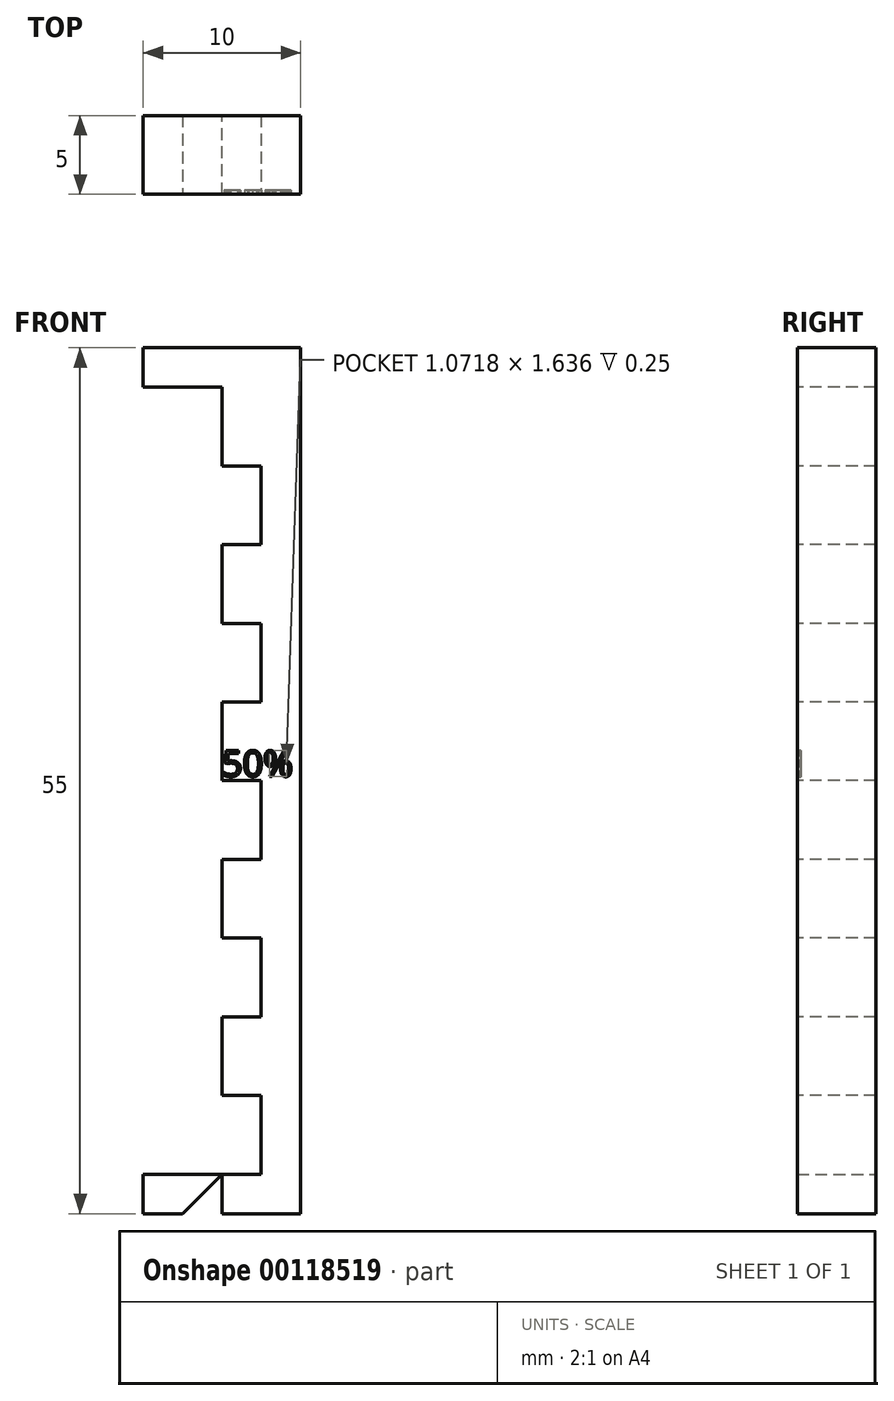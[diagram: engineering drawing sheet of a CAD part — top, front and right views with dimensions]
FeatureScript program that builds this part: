
annotation { "Feature Type Name" : "Feature", "Feature Type Description" : "" }
export const myFeature = defineFeature(function(context is Context, id is Id, definition is map)
    precondition{}
    {
        {
            var Q0;
            Q0=qCreatedBy(makeId("Front.planeOp"),FACE);
            var sketch = newSketch(context, id + "F0", { "sketchPlane" : qUnion([Q0])});
            skLineSegment(sketch, "E0.bottom", {"start": v(0, 10) * mm, "end": v(10, 10) * mm});
            skLineSegment(sketch, "E0.top", {"start": v(-10, -10) * mm, "end": v(10, -10) * mm});
            skLineSegment(sketch, "E0.left", {"start": v(-10, 0) * mm, "end": v(-10, -10) * mm});
            skLineSegment(sketch, "E0.right", {"start": v(10, 10) * mm, "end": v(10, -10) * mm});
            skLineSegment(sketch, "E1.top", {"start": v(-10, 0) * mm, "end": v(0, 0) * mm});
            skLineSegment(sketch, "E1.right", {"start": v(0, 10) * mm, "end": v(0, 0) * mm});
            skSolve(sketch);
        }
        {
            var Q0;
            Q0=makeQuery(id+"F0.imprint","IMPRINT",FACE,{"disambiguationData":[TD([[makeQuery(id+"F0.imprint","IMPRINT",EDGE,{"derivedFrom":sQuery(id+"F0.wireOp",EDGE,"E0.bottom")}),-1.0]])]});
            extrude(context, id + "F1", {"entities" : qUnion([Q0]), "oppositeDirection" : true, "depth" : 110 * mm});
        }
        {
            var Q0;
            Q0=makeQuery(id+"F1.opExtrude","CAP_FACE",FACE,{"disambiguationData":[OSD([sQuery(id+"F0.wireOp",EDGE,"E0.bottom"),sQuery(id+"F0.wireOp",EDGE,"E0.top"),sQuery(id+"F0.wireOp",EDGE,"E0.left"),sQuery(id+"F0.wireOp",EDGE,"E0.right"),sQuery(id+"F0.wireOp",EDGE,"E1.top"),sQuery(id+"F0.wireOp",EDGE,"E1.right")])],"isStart":true});
            var sketch = newSketch(context, id + "F2", { "sketchPlane" : qUnion([Q0])});
            skLineSegment(sketch, "E2.bottom", {"start": v(0, 10) * mm, "end": v(-10, 10) * mm});
            skLineSegment(sketch, "E2.top", {"start": v(0, 0) * mm, "end": v(-10, 0) * mm});
            skLineSegment(sketch, "E2.left", {"start": v(0, 10) * mm, "end": v(0, 0) * mm});
            skLineSegment(sketch, "E2.right", {"start": v(-10, 10) * mm, "end": v(-10, 0) * mm});
            skSolve(sketch);
        }
        {
            var Q0;
            Q0=qSketchRegion(id+"F2",true);
            extrude(context, id + "F3", {"entities" : qUnion([Q0]), "oppositeDirection" : true, "depth" : 5 * mm});
        }
        {
            var Q0;
            Q0=makeQuery(id+"F3.opExtrude","CAP_EDGE",EDGE,{"disambiguationData":[OSD([sQuery(id+"F2.wireOp",EDGE,"E2.left")])],"isStart":true});
            chamfer(context, id + "F4", {"entities" : qUnion([Q0]), "width" : 5 * mm, "tangentPropagation" : true});
        }
        {
            var Q0;
            Q0=makeQuery(id+"F1.opExtrude","SWEPT_FACE",FACE,{"disambiguationData":[OSD([sQuery(id+"F0.wireOp",EDGE,"E0.bottom")])]});
            var sketch = newSketch(context, id + "F5", { "sketchPlane" : qUnion([Q0])});
            skLineSegment(sketch, "E3.bottom", {"start": v(-10, 115) * mm, "end": v(5, 115) * mm});
            skLineSegment(sketch, "E3.top", {"start": v(-10, 5) * mm, "end": v(5, 5) * mm});
            skLineSegment(sketch, "E3.left", {"start": v(-10, 115) * mm, "end": v(-10, 5) * mm});
            skLineSegment(sketch, "E3.right", {"start": v(5, 115) * mm, "end": v(5, 105) * mm});
            skLineSegment(sketch, "E4.top", {"start": v(0, 15) * mm, "end": v(5, 15) * mm});
            skLineSegment(sketch, "E4.left", {"start": v(0, 85) * mm, "end": v(0, 75) * mm});
            skLineSegment(sketch, "E5.bottom", {"start": v(0, 75) * mm, "end": v(5, 75) * mm});
            skLineSegment(sketch, "E5.top", {"start": v(0, 65) * mm, "end": v(5, 65) * mm});
            skLineSegment(sketch, "E6.bottom", {"start": v(0, 55) * mm, "end": v(5, 55) * mm});
            skLineSegment(sketch, "E6.top", {"start": v(0, 45) * mm, "end": v(5, 45) * mm});
            skLineSegment(sketch, "E7.bottom", {"start": v(0, 35) * mm, "end": v(5, 35) * mm});
            skLineSegment(sketch, "E7.top", {"start": v(0, 25) * mm, "end": v(5, 25) * mm});
            skLineSegment(sketch, "E8.trimOffspring", {"start": v(5, 15) * mm, "end": v(5, 5) * mm});
            skLineSegment(sketch, "E9.trimOffspring", {"start": v(0, 25) * mm, "end": v(0, 15) * mm});
            skLineSegment(sketch, "E10.trimOffspring", {"start": v(5, 35) * mm, "end": v(5, 25) * mm});
            skLineSegment(sketch, "E11.trimOffspring", {"start": v(0, 45) * mm, "end": v(0, 35) * mm});
            skLineSegment(sketch, "E12.trimOffspring", {"start": v(5, 55) * mm, "end": v(5, 45) * mm});
            skLineSegment(sketch, "E13.trimOffspring", {"start": v(5, 75) * mm, "end": v(5, 65) * mm});
            skLineSegment(sketch, "E14.trimOffspring", {"start": v(0, 65) * mm, "end": v(0, 55) * mm});
            skLineSegment(sketch, "E15", {"start": v(0, 85) * mm, "end": v(5, 85) * mm});
            skPoint(sketch, "E16.firstSnap0", {"position": v(5, 105) * mm});
            skLineSegment(sketch, "E16.bottom", {"start": v(0, 105) * mm, "end": v(5, 105) * mm});
            skLineSegment(sketch, "E16.top", {"start": v(0, 95) * mm, "end": v(5, 95) * mm});
            skLineSegment(sketch, "E16.left", {"start": v(0, 105) * mm, "end": v(0, 95) * mm});
            skLineSegment(sketch, "E17.trimOffspring", {"start": v(5, 95) * mm, "end": v(5, 85) * mm});
            skSolve(sketch);
        }
        {
            var Q0;
            Q0=qSketchRegion(id+"F5",true);
            extrude(context, id + "F6", {"entities" : qUnion([Q0]), "operationType" : NewBodyOperationType.REMOVE, "oppositeDirection" : true, "depth" : 10 * mm});
        }
        {
            var Q0;
            Q0=makeQuery(id+"F1.opExtrude","SWEPT_FACE",FACE,{"disambiguationData":[OSD([sQuery(id+"F0.wireOp",EDGE,"E1.top")])]});
            var sketch = newSketch(context, id + "F7", { "sketchPlane" : qUnion([Q0])});
            skLineSegment(sketch, "E18.bottom", {"start": v(-10, 110) * mm, "end": v(5, 110) * mm});
            skLineSegment(sketch, "E18.top", {"start": v(-10, 105) * mm, "end": v(5, 105) * mm});
            skLineSegment(sketch, "E18.left", {"start": v(-10, 110) * mm, "end": v(-10, 105) * mm});
            skLineSegment(sketch, "E18.right", {"start": v(5, 110) * mm, "end": v(5, 105) * mm});
            skSolve(sketch);
        }
        {
            var Q0;
            Q0=qSketchRegion(id+"F7",true);
            extrude(context, id + "F8", {"entities" : qUnion([Q0]), "operationType" : NewBodyOperationType.ADD, "depth" : 10 * mm});
        }
        {
            var Q0;
            Q0=makeQuery(id+"F8.boolean.opBoolean","MERGE",FACE,{"derivedFrom":[makeQuery(id+"F1.opExtrude","SWEPT_FACE",FACE,{"disambiguationData":[OSD([sQuery(id+"F0.wireOp",EDGE,"E0.bottom")])]}),makeQuery(id+"F8.opExtrude","CAP_FACE",FACE,{"disambiguationData":[OSD([sQuery(id+"F7.wireOp",EDGE,"E18.bottom"),sQuery(id+"F7.wireOp",EDGE,"E18.top"),sQuery(id+"F7.wireOp",EDGE,"E18.left"),sQuery(id+"F7.wireOp",EDGE,"E18.right")])],"isStart":false})]});
            var sketch = newSketch(context, id + "F9", { "sketchPlane" : qUnion([Q0])});
            skText(sketch, "E19", { "text": "50%", "fontName": "OpenSans-Regular.ttf"});
            const initialGuessF9  = {"E19": [0, 0.05554, 1, 0, 0.0033]};
            skSetInitialGuess(sketch, initialGuessF9);
            skSolve(sketch);
        }
        {
            var Q0;
            Q0=qSketchRegion(id+"F9",true);
            extrude(context, id + "F10", {"entities" : qUnion([Q0]), "operationType" : NewBodyOperationType.REMOVE, "oppositeDirection" : true, "depth" : 0.5 * mm});
        }
        {
            var Q0;
            Q0=makeQuery(id+"F1.opExtrude","SWEPT_BODY",BODY,{"disambiguationData":[OSD([sQuery(id+"F0.wireOp",EDGE,"E0.bottom"),sQuery(id+"F0.wireOp",EDGE,"E0.top"),sQuery(id+"F0.wireOp",EDGE,"E0.left"),sQuery(id+"F0.wireOp",EDGE,"E0.right"),sQuery(id+"F0.wireOp",EDGE,"E1.top"),sQuery(id+"F0.wireOp",EDGE,"E1.right")])]});
            var Q1;
            Q1=makeQuery(id+"F3.opExtrude","SWEPT_BODY",BODY,{"disambiguationData":[OSD([sQuery(id+"F2.wireOp",EDGE,"E2.bottom"),sQuery(id+"F2.wireOp",EDGE,"E2.top"),sQuery(id+"F2.wireOp",EDGE,"E2.left"),sQuery(id+"F2.wireOp",EDGE,"E2.right")])]});
            var Q2;
            Q2=qCreatedBy(makeId("Origin.pointOp"),VERTEX);
            transform(context, id + "F11", {"entities" : qUnion([Q0, Q1]), "transformType" : TransformType.SCALE_UNIFORMLY, "scale" : 0.5, "makeCopy" : false, "scalePoint" : qUnion([Q2])});
        }
        {
            var Q0;
            Q0=makeQuery(id+"F1.opExtrude","SWEPT_BODY",BODY,{"disambiguationData":[OSD([sQuery(id+"F0.wireOp",EDGE,"E0.bottom"),sQuery(id+"F0.wireOp",EDGE,"E0.top"),sQuery(id+"F0.wireOp",EDGE,"E0.left"),sQuery(id+"F0.wireOp",EDGE,"E0.right"),sQuery(id+"F0.wireOp",EDGE,"E1.top"),sQuery(id+"F0.wireOp",EDGE,"E1.right")])]});
            var Q1;
            Q1=makeQuery(id+"F3.opExtrude","SWEPT_BODY",BODY,{"disambiguationData":[OSD([sQuery(id+"F2.wireOp",EDGE,"E2.bottom"),sQuery(id+"F2.wireOp",EDGE,"E2.top"),sQuery(id+"F2.wireOp",EDGE,"E2.left"),sQuery(id+"F2.wireOp",EDGE,"E2.right")])]});
            var Q2;
            Q2=makeQuery(id+"F1.opExtrude","CAP_EDGE",EDGE,{"disambiguationData":[OSD([sQuery(id+"F0.wireOp",EDGE,"E1.top")])],"isStart":true});
            transform(context, id + "F12", {"entities" : qUnion([Q0, Q1]), "transformType" : TransformType.ROTATION, "transformAxis" : qUnion([Q2]), "angle" : 90 * degree, "makeCopy" : false});
        }
        {
            var Q0;
            Q0=makeQuery(id+"F1.opExtrude","SWEPT_FACE",FACE,{"disambiguationData":[OSD([sQuery(id+"F0.wireOp",EDGE,"E0.top")])]});
            var Q1;
            Q1=makeQuery(id+"F1.opExtrude","SWEPT_FACE",FACE,{"disambiguationData":[OSD([sQuery(id+"F0.wireOp",EDGE,"E1.top")])]});
            extrude(context, id + "F13", {"entities" : qUnion([Q0]), "operationType" : NewBodyOperationType.REMOVE, "endBound" : BoundingType.UP_TO_SURFACE, "oppositeDirection" : true, "endBoundEntityFace" : qUnion([Q1]), "depth" : 1 * mm});
        }
    });
